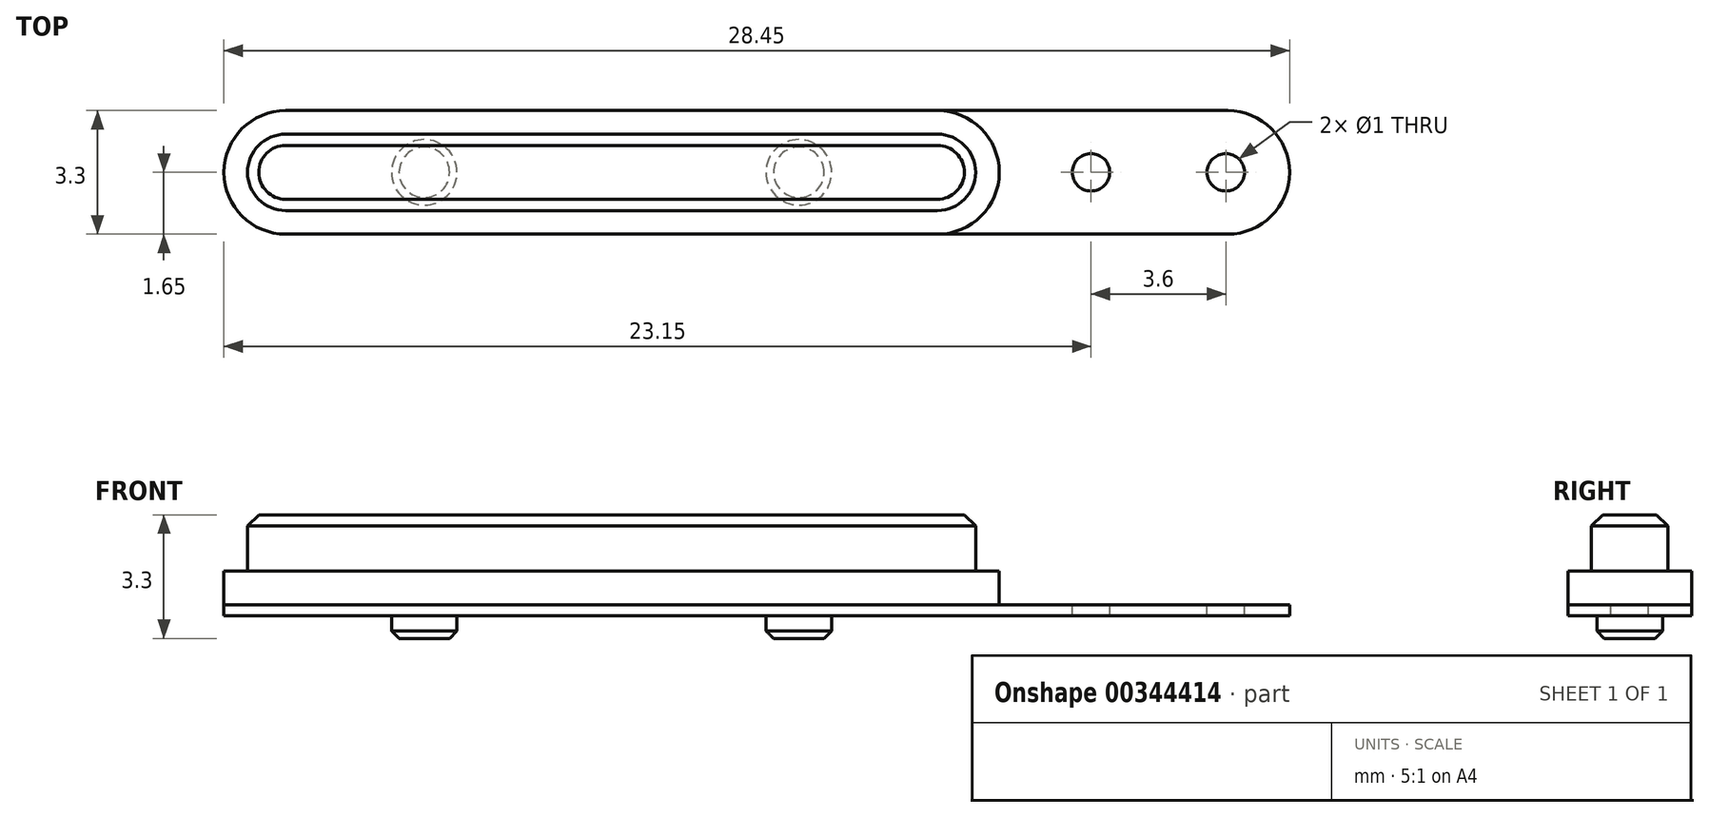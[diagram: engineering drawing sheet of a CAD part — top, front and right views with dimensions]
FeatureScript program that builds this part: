
annotation { "Feature Type Name" : "Feature", "Feature Type Description" : "" }
export const myFeature = defineFeature(function(context is Context, id is Id, definition is map)
    precondition{}
    {
        {
            var Q0;
            Q0=qCreatedBy(makeId("Top.planeOp"),FACE);
            var sketch = newSketch(context, id + "F0", { "sketchPlane" : qUnion([Q0])});
            skLineSegment(sketch, "E0", {"start": v(-8.7, 1.02) * mm, "end": v(8.7, 1.02) * mm});
            skLineSegment(sketch, "E1", {"start": v(-8.7, -1.02) * mm, "end": v(8.7, -1.02) * mm});
            skLineSegment(sketch, "E2", {"start": v(-8.7, 1.02) * mm, "end": v(-8.7, -1.02) * mm, "construction": true});
            skArc(sketch, "E3", {"start": v(-8.7, 1.02) * mm, "mid": v(-9.72, 0) * mm, "end": v(-8.7, -1.02) * mm});
            skLineSegment(sketch, "E4", {"start": v(8.7, 1.02) * mm, "end": v(8.7, -1.02) * mm, "construction": true});
            skArc(sketch, "E5", {"start": v(8.7, 1.02) * mm, "mid": v(9.72, 0) * mm, "end": v(8.7, -1.02) * mm});
            skSolve(sketch);
        }
        {
            var Q0;
            Q0 = qSketchRegion(id + "F0", true);
            extrude(context, id + "F1", {"entities" : qUnion([Q0]), "depth" : 1.5 * mm});
        }
        {
            var Q0;
            Q0=makeQuery(id+"F1.opExtrude","CAP_FACE",FACE,{"disambiguationData":[OSD([sQuery(id+"F0.wireOp",EDGE,"E0"),sQuery(id+"F0.wireOp",EDGE,"E1"),sQuery(id+"F0.wireOp",EDGE,"E3"),sQuery(id+"F0.wireOp",EDGE,"E5")])],"isStart":false});
            chamfer(context, id + "F2", {"entities" : qUnion([Q0]), "width" : 0.3 * mm, "tangentPropagation" : true});
        }
        {
            var Q0;
            Q0=qCreatedBy(makeId("Top.planeOp"),FACE);
            var sketch = newSketch(context, id + "F3", { "sketchPlane" : qUnion([Q0])});
            skLineSegment(sketch, "E6", {"start": v(-8.7, -1.65) * mm, "end": v(8.7, -1.65) * mm});
            skLineSegment(sketch, "E7", {"start": v(-8.7, 1.65) * mm, "end": v(8.7, 1.65) * mm});
            skLineSegment(sketch, "E8", {"start": v(-8.7, -1.65) * mm, "end": v(-8.7, 1.65) * mm, "construction": true});
            skLineSegment(sketch, "E9", {"start": v(8.7, -1.65) * mm, "end": v(8.7, 1.65) * mm, "construction": true});
            skArc(sketch, "E10", {"start": v(-8.7, -1.65) * mm, "mid": v(-10.35, 0) * mm, "end": v(-8.7, 1.65) * mm});
            skArc(sketch, "E11", {"start": v(8.7, -1.65) * mm, "mid": v(10.35, 0) * mm, "end": v(8.7, 1.65) * mm});
            skSolve(sketch);
        }
        {
            var Q0;
            Q0 = qSketchRegion(id + "F3", true);
            extrude(context, id + "F4", {"entities" : qUnion([Q0]), "operationType" : NewBodyOperationType.ADD, "oppositeDirection" : true, "depth" : 0.9 * mm});
        }
        {
            var Q0;
            Q0=makeQuery(id+"F4.opExtrude","CAP_FACE",FACE,{"disambiguationData":[OSD([sQuery(id+"F3.wireOp",EDGE,"E6"),sQuery(id+"F3.wireOp",EDGE,"E7"),sQuery(id+"F3.wireOp",EDGE,"E10"),sQuery(id+"F3.wireOp",EDGE,"E11")])],"isStart":false});
            var sketch = newSketch(context, id + "F5", { "sketchPlane" : qUnion([Q0])});
            skArc(sketch, "E12", {"start": v(-8.7, 1.65) * mm, "mid": v(-10.35, 0) * mm, "end": v(-8.7, -1.65) * mm});
            skLineSegment(sketch, "E13", {"start": v(-8.7, 1.65) * mm, "end": v(16.45, 1.65) * mm});
            skLineSegment(sketch, "E14", {"start": v(-8.7, -1.65) * mm, "end": v(16.45, -1.65) * mm});
            skLineSegment(sketch, "E15", {"start": v(16.45, 1.65) * mm, "end": v(16.45, -1.65) * mm, "construction": true});
            skArc(sketch, "E16", {"start": v(16.45, 1.65) * mm, "mid": v(18.1, 0) * mm, "end": v(16.45, -1.65) * mm});
            skCircle(sketch, "E17", {"center": v(12.8, 0) * mm, "radius": 0.5 * mm});
            skCircle(sketch, "E18", {"center": v(16.4, 0) * mm, "radius": 0.5 * mm});
            skSolve(sketch);
        }
        {
            var Q0;
            Q0 = qSketchRegion(id + "F5", true);
            extrude(context, id + "F6", {"entities" : qUnion([Q0]), "depth" : 0.3 * mm});
        }
        {
            var Q0;
            Q0=makeQuery(id+"F6.opExtrude","CAP_FACE",FACE,{"disambiguationData":[OSD([sQuery(id+"F5.wireOp",EDGE,"E12"),sQuery(id+"F5.wireOp",EDGE,"E13"),sQuery(id+"F5.wireOp",EDGE,"E14"),sQuery(id+"F5.wireOp",EDGE,"E16"),sQuery(id+"F5.wireOp",EDGE,"E17"),sQuery(id+"F5.wireOp",EDGE,"E18")])],"isStart":false});
            var sketch = newSketch(context, id + "F7", { "sketchPlane" : qUnion([Q0])});
            skCircle(sketch, "E19", {"center": v(-5, 0) * mm, "radius": 0.88 * mm});
            skCircle(sketch, "E20", {"center": v(5, 0) * mm, "radius": 0.88 * mm});
            skSolve(sketch);
        }
        {
            var Q0;
            Q0 = qSketchRegion(id + "F7", true);
            extrude(context, id + "F8", {"entities" : qUnion([Q0]), "operationType" : NewBodyOperationType.ADD, "depth" : 0.6 * mm});
        }
        {
            var Q0;
            Q0=makeQuery(id+"F8.opExtrude","CAP_EDGE",EDGE,{"disambiguationData":[OSD([sQuery(id+"F7.wireOp",EDGE,"E19")])],"isStart":false});
            var Q1;
            Q1=makeQuery(id+"F8.opExtrude","CAP_EDGE",EDGE,{"disambiguationData":[OSD([sQuery(id+"F7.wireOp",EDGE,"E20")])],"isStart":false});
            chamfer(context, id + "F9", {"entities" : qUnion([Q0, Q1]), "width" : 0.2 * mm, "tangentPropagation" : true});
        }
    });
